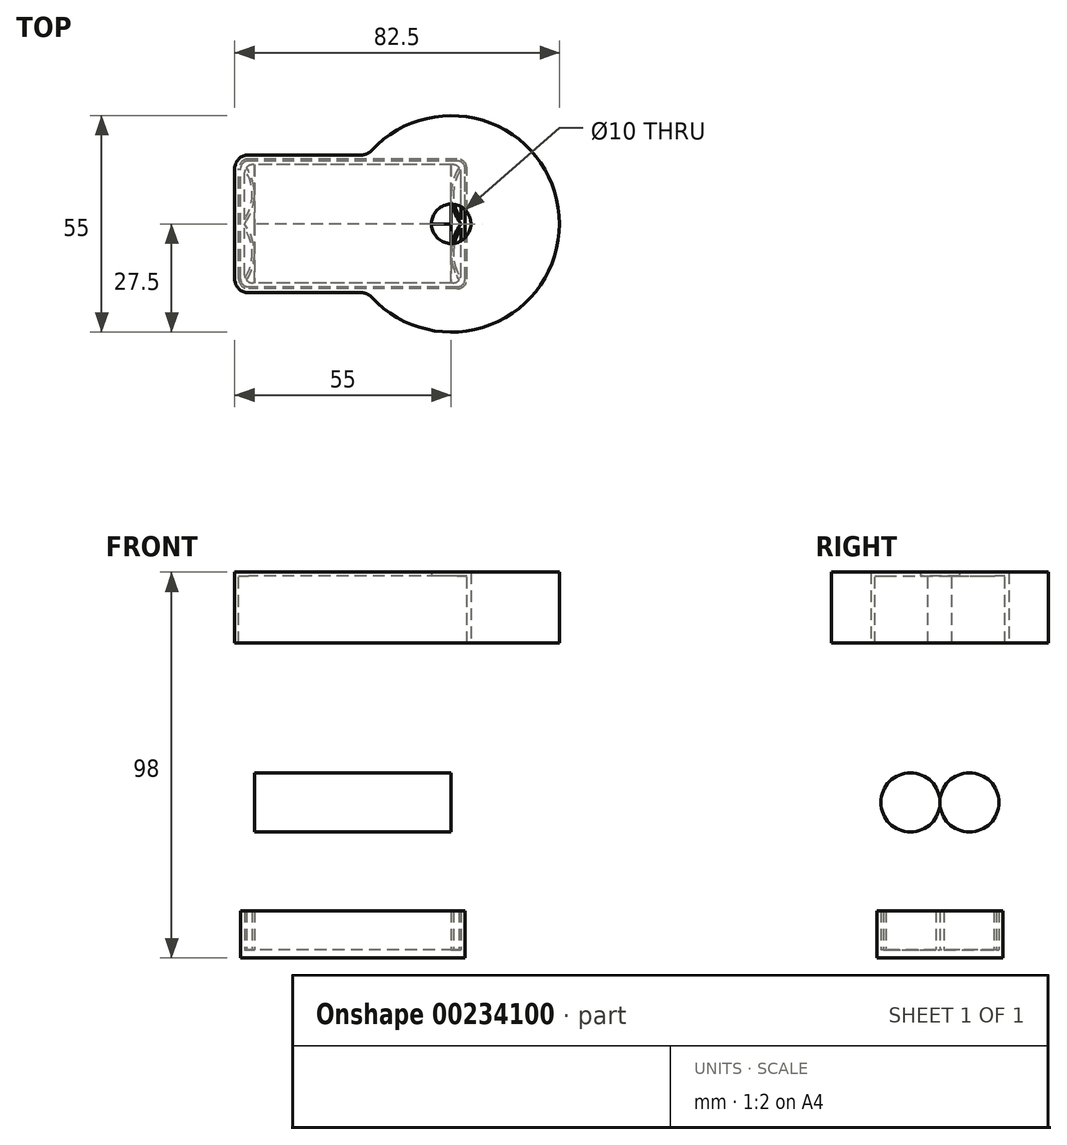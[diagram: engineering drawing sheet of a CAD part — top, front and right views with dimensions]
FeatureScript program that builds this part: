
annotation { "Feature Type Name" : "Feature", "Feature Type Description" : "" }
export const myFeature = defineFeature(function(context is Context, id is Id, definition is map)
    precondition{}
    {
        {
            var Q0;
            Q0=qCreatedBy(makeId("Top.planeOp"),FACE);
            var sketch = newSketch(context, id + "F0", { "sketchPlane" : qUnion([Q0])});
            skLineSegment(sketch, "E0.bottom", {"start": v(28.5, -16) * mm, "end": v(-28.5, -16) * mm});
            skLineSegment(sketch, "E0.top", {"start": v(28.5, 16) * mm, "end": v(-28.5, 16) * mm});
            skLineSegment(sketch, "E0.left", {"start": v(28.5, -16) * mm, "end": v(28.5, 16) * mm});
            skLineSegment(sketch, "E0.right", {"start": v(-28.5, -16) * mm, "end": v(-28.5, 16) * mm});
            skPoint(sketch, "E0.middle", {"position": v(0, 0) * mm});
            skLineSegment(sketch, "E1.bottom", {"start": v(27.5, -15) * mm, "end": v(-27.5, -15) * mm});
            skLineSegment(sketch, "E1.top", {"start": v(27.5, 15) * mm, "end": v(-27.5, 15) * mm});
            skLineSegment(sketch, "E1.left", {"start": v(27.5, -15) * mm, "end": v(27.5, 15) * mm});
            skLineSegment(sketch, "E1.right", {"start": v(-27.5, -15) * mm, "end": v(-27.5, 15) * mm});
            skSolve(sketch);
        }
        {
            var Q0;
            Q0=makeQuery(id+"F0.imprint","IMPRINT",FACE,{"disambiguationData":[TD([[makeQuery(id+"F0.imprint","IMPRINT",EDGE,{"derivedFrom":sQuery(id+"F0.wireOp",EDGE,"E0.bottom")}),-1.0]])]});
            var Q1;
            Q1=makeQuery(id+"F0.imprint","IMPRINT",FACE,{"disambiguationData":[TD([[makeQuery(id+"F0.imprint","IMPRINT",EDGE,{"derivedFrom":sQuery(id+"F0.wireOp",EDGE,"E1.bottom")}),-1.0]])]});
            extrude(context, id + "F1", {"entities" : qUnion([Q0, Q1]), "oppositeDirection" : true, "depth" : 2 * mm});
        }
        {
            var Q0;
            Q0=makeQuery(id+"F0.imprint","IMPRINT",FACE,{"disambiguationData":[TD([[makeQuery(id+"F0.imprint","IMPRINT",EDGE,{"derivedFrom":sQuery(id+"F0.wireOp",EDGE,"511JZqgd-saJz-wMDc-ROUc-2f22ZJkLcz4P.bottom")}),-1.0]])]});
            var Q1;
            {var subQ0=sQuery(id+"F0.wireOp",EDGE,"E0.bottom");Q1=makeQuery(id+"F0.imprint","IMPRINT",FACE,{"disambiguationData":[TD([[makeQuery(id+"F0.imprint","IMPRINT",EDGE,{"derivedFrom":subQ0}),-1.0]])]});}
            extrude(context, id + "F2", {"entities" : qUnion([Q0, Q1]), "operationType" : NewBodyOperationType.ADD, "depth" : 10 * mm});
        }
        {
            var Q0;
            Q0=makeQuery(id+"F2.opExtrude","SWEPT_EDGE",EDGE,{"disambiguationData":[OSD([sQuery(id+"F0.wireOp",EDGE,"E1.top"),sQuery(id+"F0.wireOp",EDGE,"E1.right")])]});
            var Q1;
            {var subQ0=sQuery(id+"F0.wireOp",EDGE,"E0.right");var subQ1=sQuery(id+"F0.wireOp",EDGE,"E0.top");Q1=makeQuery(id+"F2.boolean.opBoolean","MERGE",EDGE,{"derivedFrom":[makeQuery(id+"F1.opExtrude","SWEPT_EDGE",EDGE,{"disambiguationData":[OSD([subQ1,subQ0])]}),makeQuery(id+"F2.opExtrude","SWEPT_EDGE",EDGE,{"disambiguationData":[OSD([subQ1,subQ0])]})]});}
            var Q2;
            Q2=makeQuery(id+"F2.opExtrude","SWEPT_EDGE",EDGE,{"disambiguationData":[OSD([sQuery(id+"F0.wireOp",EDGE,"E1.bottom"),sQuery(id+"F0.wireOp",EDGE,"E1.right")])]});
            var Q3;
            {var subQ0=sQuery(id+"F0.wireOp",EDGE,"E0.left");var subQ1=sQuery(id+"F0.wireOp",EDGE,"E0.top");Q3=makeQuery(id+"F2.boolean.opBoolean","MERGE",EDGE,{"derivedFrom":[makeQuery(id+"F1.opExtrude","SWEPT_EDGE",EDGE,{"disambiguationData":[OSD([subQ1,subQ0])]}),makeQuery(id+"F2.opExtrude","SWEPT_EDGE",EDGE,{"disambiguationData":[OSD([subQ1,subQ0])]})]});}
            var Q4;
            {var subQ0=sQuery(id+"F0.wireOp",EDGE,"E0.right");var subQ1=sQuery(id+"F0.wireOp",EDGE,"E0.bottom");Q4=makeQuery(id+"F2.boolean.opBoolean","MERGE",EDGE,{"derivedFrom":[makeQuery(id+"F1.opExtrude","SWEPT_EDGE",EDGE,{"disambiguationData":[OSD([subQ1,subQ0])]}),makeQuery(id+"F2.opExtrude","SWEPT_EDGE",EDGE,{"disambiguationData":[OSD([subQ1,subQ0])]})]});}
            var Q5;
            Q5=makeQuery(id+"F2.opExtrude","SWEPT_EDGE",EDGE,{"disambiguationData":[OSD([sQuery(id+"F0.wireOp",EDGE,"E1.top"),sQuery(id+"F0.wireOp",EDGE,"E1.left")])]});
            var Q6;
            Q6=makeQuery(id+"F2.opExtrude","SWEPT_EDGE",EDGE,{"disambiguationData":[OSD([sQuery(id+"F0.wireOp",EDGE,"E1.bottom"),sQuery(id+"F0.wireOp",EDGE,"E1.left")])]});
            var Q7;
            {var subQ0=sQuery(id+"F0.wireOp",EDGE,"E0.left");var subQ1=sQuery(id+"F0.wireOp",EDGE,"E0.bottom");Q7=makeQuery(id+"F2.boolean.opBoolean","MERGE",EDGE,{"derivedFrom":[makeQuery(id+"F1.opExtrude","SWEPT_EDGE",EDGE,{"disambiguationData":[OSD([subQ1,subQ0])]}),makeQuery(id+"F2.opExtrude","SWEPT_EDGE",EDGE,{"disambiguationData":[OSD([subQ1,subQ0])]})]});}
            var Q8;
            Q8=makeQuery(id+"F2.opExtrude","CAP_EDGE",EDGE,{"disambiguationData":[OSD([sQuery(id+"F0.wireOp",EDGE,"E1.top")])],"isStart":true});
            var Q9;
            Q9=makeQuery(id+"F2.opExtrude","CAP_EDGE",EDGE,{"disambiguationData":[OSD([sQuery(id+"F0.wireOp",EDGE,"E1.bottom")])],"isStart":true});
            fillet(context, id + "F3", {"entities" : qUnion([Q0, Q1, Q2, Q3, Q4, Q5, Q6, Q7, Q8, Q9]), "radius" : 2 * mm, "tangentPropagation" : true, "allowEdgeOverflow" : false});
        }
        {
            var Q0;
            Q0=qCreatedBy(makeId("Right.planeOp"),FACE);
            var sketch = newSketch(context, id + "F4", { "sketchPlane" : qUnion([Q0])});
            skCircle(sketch, "E2", {"center": v(-7.5, 7.5) * mm, "radius": 7.5 * mm});
            skCircle(sketch, "E3.MirrorC", {"center": v(7.5, 7.5) * mm, "radius": 7.5 * mm});
            skSolve(sketch);
        }
        {
            var Q0;
            Q0 = qSketchRegion(id + "F4", true);
            extrude(context, id + "F5", {"entities" : qUnion([Q0]), "endBound" : BoundingType.SYMMETRIC, "depth" : 50 * mm});
        }
        {
            var Q0;
            Q0=qCreatedBy(makeId("Top.planeOp"),FACE);
            var sketch = newSketch(context, id + "F6", { "sketchPlane" : qUnion([Q0])});
            skLineSegment(sketch, "E4.0", {"start": v(-27.5, -15) * mm, "end": v(-27.5, 15) * mm, "construction": true});
            skLineSegment(sketch, "E5.0", {"start": v(-25, 0) * mm, "end": v(-25, 15) * mm, "construction": true});
            skArc(sketch, "E6", {"start": v(-27.5, 0) * mm, "mid": v(-25, 7.5) * mm, "end": v(-27.5, 15) * mm});
            skArc(sketch, "E7", {"start": v(-27.5, 1.05) * mm, "mid": v(-25.6, 7.5) * mm, "end": v(-27.5, 13.95) * mm});
            skLineSegment(sketch, "E8", {"start": v(-27.5, 15) * mm, "end": v(-27.5, 13.95) * mm});
            skLineSegment(sketch, "E9", {"start": v(-27.5, 1.05) * mm, "end": v(-27.5, 0) * mm});
            skLineSegment(sketch, "E10.MirrorCS", {"start": v(-27.5, -15) * mm, "end": v(-27.5, -13.95) * mm});
            skArc(sketch, "E11.MirrorCS", {"start": v(-27.5, -1.05) * mm, "mid": v(-25.6, -7.5) * mm, "end": v(-27.5, -13.95) * mm});
            skArc(sketch, "E12.MirrorCS", {"start": v(-27.5, 0) * mm, "mid": v(-25, -7.5) * mm, "end": v(-27.5, -15) * mm});
            skLineSegment(sketch, "E13.MirrorCS", {"start": v(-27.5, -1.05) * mm, "end": v(-27.5, 0) * mm});
            skLineSegment(sketch, "E14.MirrorCS", {"start": v(-25, 0) * mm, "end": v(-25, -15) * mm, "construction": true});
            skLineSegment(sketch, "E15.MirrorCS", {"start": v(27.5, -1.05) * mm, "end": v(27.5, 0) * mm});
            skLineSegment(sketch, "E16.MirrorCS", {"start": v(27.5, -15) * mm, "end": v(27.5, -13.95) * mm});
            skLineSegment(sketch, "E17.MirrorCS", {"start": v(27.5, 15) * mm, "end": v(27.5, 13.95) * mm});
            skLineSegment(sketch, "E18.MirrorCS", {"start": v(27.5, 1.05) * mm, "end": v(27.5, 0) * mm});
            skLineSegment(sketch, "E19.MirrorCS", {"start": v(27.5, -15) * mm, "end": v(27.5, 15) * mm, "construction": true});
            skLineSegment(sketch, "E20.MirrorCS", {"start": v(25, 0) * mm, "end": v(25, -15) * mm, "construction": true});
            skArc(sketch, "E21.MirrorCS", {"start": v(27.5, 0) * mm, "mid": v(25, -7.5) * mm, "end": v(27.5, -15) * mm});
            skArc(sketch, "E22.MirrorCS", {"start": v(27.5, 0) * mm, "mid": v(25, 7.5) * mm, "end": v(27.5, 15) * mm});
            skLineSegment(sketch, "E23.MirrorCS", {"start": v(25, 0) * mm, "end": v(25, 15) * mm, "construction": true});
            skArc(sketch, "E24.MirrorCS", {"start": v(27.5, 1.05) * mm, "mid": v(25.6, 7.5) * mm, "end": v(27.5, 13.95) * mm});
            skArc(sketch, "E25.MirrorCS", {"start": v(27.5, -1.05) * mm, "mid": v(25.6, -7.5) * mm, "end": v(27.5, -13.95) * mm});
            skSolve(sketch);
        }
        {
            var Q0;
            Q0=makeQuery(id+"F6.imprint","IMPRINT",FACE,{"disambiguationData":[TD([[makeQuery(id+"F6.imprint","IMPRINT",EDGE,{"derivedFrom":sQuery(id+"F6.wireOp",EDGE,"E6")}),1.0]])]});
            var Q1;
            Q1=makeQuery(id+"F6.imprint","IMPRINT",FACE,{"disambiguationData":[TD([[makeQuery(id+"F6.imprint","IMPRINT",EDGE,{"derivedFrom":sQuery(id+"F6.wireOp",EDGE,"E10.MirrorCS")}),-1.0]])]});
            var Q2;
            Q2=makeQuery(id+"F6.imprint","IMPRINT",FACE,{"disambiguationData":[TD([[makeQuery(id+"F6.imprint","IMPRINT",EDGE,{"derivedFrom":sQuery(id+"F6.wireOp",EDGE,"E17.MirrorCS")}),-1.0]])]});
            var Q3;
            Q3=makeQuery(id+"F6.imprint","IMPRINT",FACE,{"disambiguationData":[TD([[makeQuery(id+"F6.imprint","IMPRINT",EDGE,{"derivedFrom":sQuery(id+"F6.wireOp",EDGE,"E15.MirrorCS")}),1.0]])]});
            extrude(context, id + "F7", {"entities" : qUnion([Q0, Q1, Q2, Q3]), "operationType" : NewBodyOperationType.ADD, "depth" : 10 * mm});
        }
        {
            var Q0;
            Q0=qCreatedBy(makeId("Top.planeOp"),FACE);
            cPlane(context, id + "F8", {"entities" : qUnion([Q0]), "cplaneType" : CPlaneType.OFFSET, "offset" : 15 * mm, "width" : 150 * mm, "height" : 150 * mm});
        }
        {
            var Q0;
            Q0=qCreatedBy(id+"F8.planeOp",FACE);
            var sketch = newSketch(context, id + "F9", { "sketchPlane" : qUnion([Q0])});
            skLineSegment(sketch, "E26.bottom", {"start": v(26.5, -16.5) * mm, "end": v(-26.5, -16.5) * mm});
            skLineSegment(sketch, "E26.top", {"start": v(26.5, 16.5) * mm, "end": v(-26.5, 16.5) * mm});
            skLineSegment(sketch, "E26.left", {"start": v(29, -14) * mm, "end": v(29, 14) * mm});
            skLineSegment(sketch, "E26.right", {"start": v(-29, -14) * mm, "end": v(-29, 14) * mm});
            skPoint(sketch, "E26.middle", {"position": v(0, 0) * mm});
            skPoint(sketch, "E27.visualSharp", {"position": v(-29, 16.5) * mm});
            skArc(sketch, "E27.filletArc", {"start": v(-26.5, 16.5) * mm, "mid": v(-28.27, 15.77) * mm, "end": v(-29, 14) * mm});
            skPoint(sketch, "E28.visualSharp", {"position": v(29, 16.5) * mm});
            skArc(sketch, "E28.filletArc", {"start": v(29, 14) * mm, "mid": v(28.27, 15.77) * mm, "end": v(26.5, 16.5) * mm});
            skPoint(sketch, "E29.visualSharp", {"position": v(29, -16.5) * mm});
            skArc(sketch, "E29.filletArc", {"start": v(26.5, -16.5) * mm, "mid": v(28.27, -15.77) * mm, "end": v(29, -14) * mm});
            skPoint(sketch, "E30.visualSharp", {"position": v(-29, -16.5) * mm});
            skArc(sketch, "E30.filletArc", {"start": v(-29, -14) * mm, "mid": v(-28.27, -15.77) * mm, "end": v(-26.5, -16.5) * mm});
            skLineSegment(sketch, "E31.bottom", {"start": v(2.2, -17.5) * mm, "end": v(-26.5, -17.5) * mm});
            skLineSegment(sketch, "E31.top", {"start": v(2.2, 17.5) * mm, "end": v(-26.5, 17.5) * mm});
            skLineSegment(sketch, "E31.left", {"start": v(30, -27.04) * mm, "end": v(30, 27.04) * mm});
            skLineSegment(sketch, "E31.right", {"start": v(-30, -14) * mm, "end": v(-30, 14) * mm});
            skPoint(sketch, "E32.visualSharp", {"position": v(-30, 17.5) * mm});
            skArc(sketch, "E32.filletArc", {"start": v(-26.5, 17.5) * mm, "mid": v(-28.97, 16.47) * mm, "end": v(-30, 14) * mm});
            skPoint(sketch, "E33.visualSharp", {"position": v(-30, -17.5) * mm});
            skArc(sketch, "E33.filletArc", {"start": v(-30, -14) * mm, "mid": v(-28.97, -16.47) * mm, "end": v(-26.5, -17.5) * mm});
            skArc(sketch, "E34", {"start": v(4.77, -18.63) * mm, "mid": v(52.5, 0) * mm, "end": v(4.77, 18.63) * mm});
            skPoint(sketch, "E35.orphan", {"position": v(30, 17.5) * mm});
            skPoint(sketch, "E36.orphan", {"position": v(30, -17.5) * mm});
            skCircle(sketch, "E37", {"center": v(25, 0) * mm, "radius": 5 * mm});
            skPoint(sketch, "E38.visualSharp", {"position": v(3.79, 17.5) * mm});
            skArc(sketch, "E38.filletArc", {"start": v(2.2, 17.5) * mm, "mid": v(3.6, 17.8) * mm, "end": v(4.77, 18.63) * mm});
            skPoint(sketch, "E39.visualSharp", {"position": v(3.79, -17.5) * mm});
            skArc(sketch, "E39.filletArc", {"start": v(4.77, -18.63) * mm, "mid": v(3.6, -17.8) * mm, "end": v(2.2, -17.5) * mm});
            skSolve(sketch);
        }
        {
            var Q0;
            Q0=makeQuery(id+"F9.imprint","IMPRINT",FACE,{"disambiguationData":[TD([[makeQuery(id+"F9.imprint","IMPRINT",EDGE,{"derivedFrom":sQuery(id+"F9.wireOp",EDGE,"E26.bottom")}),-1.0]])]});
            var Q1;
            Q1=makeQuery(id+"F9.imprint","IMPRINT",FACE,{"disambiguationData":[TD([[makeQuery(id+"F9.imprint","IMPRINT",EDGE,{"derivedFrom":sQuery(id+"F9.wireOp",EDGE,"E26.bottom")}),1.0]])]});
            var Q2;
            {var subQ0=sQuery(id+"F9.wireOp",EDGE,"E34");var subQ1=sQuery(id+"F9.wireOp",EDGE,"E31.left");var subQ2=makeQuery(id+"F9.imprint","INTERSECT",VERTEX,{"disambiguationData":[OD(0.0)],"derivedFrom":[subQ1,subQ0]});Q2=makeQuery(id+"F9.imprint","IMPRINT",FACE,{"disambiguationData":[TD([[makeQuery(id+"F9.imprint","IMPRINT",EDGE,{"disambiguationData":[TD([[subQ2,-1.0]])],"derivedFrom":subQ1}),-1.0]])]});}
            extrude(context, id + "F10", {"entities" : qUnion([Q0, Q1, Q2]), "depth" : 1 * mm});
        }
        {
            var Q0;
            Q0 = qSketchRegion(id + "F9", true);
            var Q1;
            {var subQ0=sQuery(id+"F9.wireOp",EDGE,"E37");var subQ1=sQuery(id+"F9.wireOp",EDGE,"E26.left");var subQ2=makeQuery(id+"F9.imprint","INTERSECT",VERTEX,{"disambiguationData":[OD(0.0)],"derivedFrom":[subQ1,subQ0]});Q1=makeQuery(id+"F9.imprint","IMPRINT",FACE,{"disambiguationData":[TD([[makeQuery(id+"F9.imprint","IMPRINT",EDGE,{"disambiguationData":[TD([[subQ2,-1.0]])],"derivedFrom":subQ1}),-1.0]])]});}
            extrude(context, id + "F11", {"entities" : qUnion([Q0, Q1]), "operationType" : NewBodyOperationType.ADD, "oppositeDirection" : true, "depth" : 17 * mm});
        }
        {
            var Q0;
            Q0=makeQuery(id+"F10.opExtrude","SWEPT_BODY",BODY,{"disambiguationData":[OSD([sQuery(id+"F9.wireOp",EDGE,"E31.bottom"),sQuery(id+"F9.wireOp",EDGE,"E31.top"),sQuery(id+"F9.wireOp",EDGE,"E31.right"),sQuery(id+"F9.wireOp",EDGE,"E32.filletArc"),sQuery(id+"F9.wireOp",EDGE,"E33.filletArc"),sQuery(id+"F9.wireOp",EDGE,"E34"),sQuery(id+"F9.wireOp",EDGE,"E37"),sQuery(id+"F9.wireOp",EDGE,"E38.filletArc"),sQuery(id+"F9.wireOp",EDGE,"E39.filletArc")])]});
            transform(context, id + "F12", {"entities" : qUnion([Q0]), "transformType" : TransformType.TRANSLATION_3D, "dx" : 0 * mm, "dy" : 0 * mm, "dz" : 50 * mm, "makeCopy" : false});
        }
        {
            var Q0;
            Q0=makeQuery(id+"F1.opExtrude","SWEPT_BODY",BODY,{"disambiguationData":[OSD([sQuery(id+"F0.wireOp",EDGE,"E0.bottom"),sQuery(id+"F0.wireOp",EDGE,"E0.top"),sQuery(id+"F0.wireOp",EDGE,"E0.left"),sQuery(id+"F0.wireOp",EDGE,"E0.right")])]});
            transform(context, id + "F13", {"entities" : qUnion([Q0]), "transformType" : TransformType.TRANSLATION_3D, "dx" : 0 * mm, "dy" : 0 * mm, "dz" : -30 * mm, "makeCopy" : false});
        }
    });
